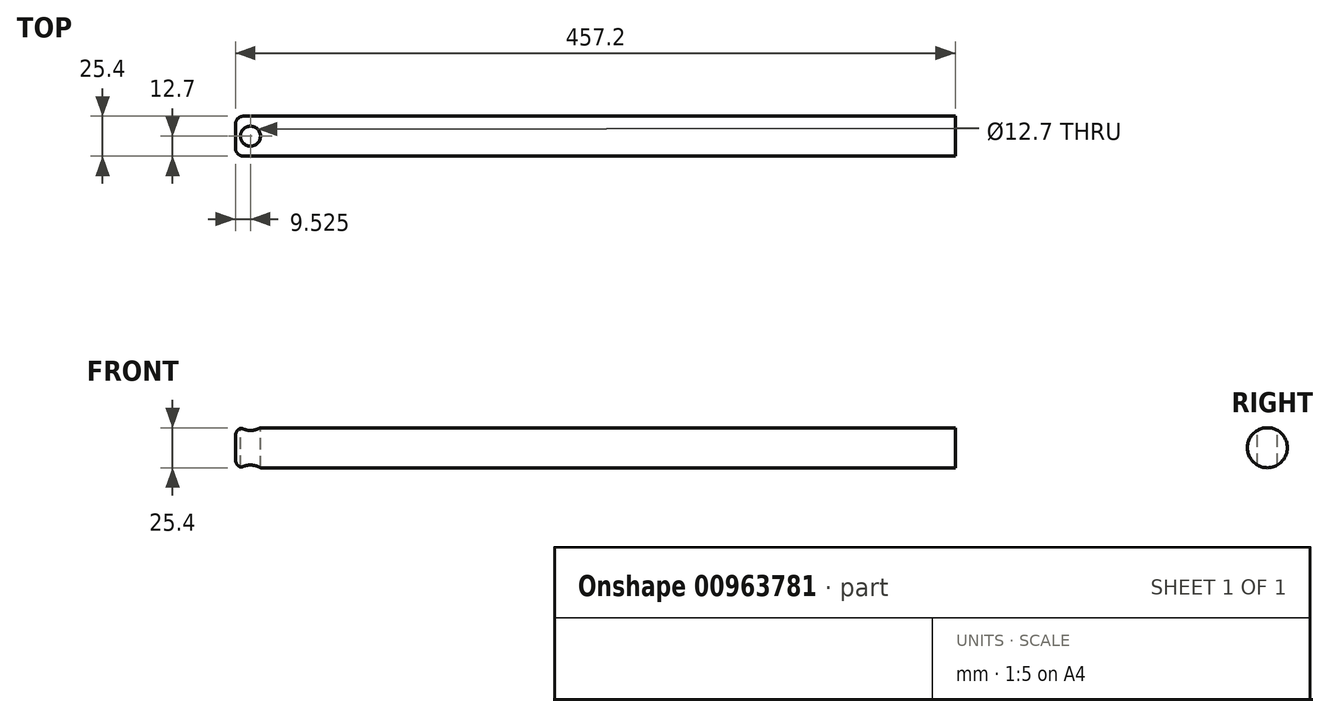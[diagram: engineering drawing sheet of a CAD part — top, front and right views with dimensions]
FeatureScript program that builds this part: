
annotation { "Feature Type Name" : "Feature", "Feature Type Description" : "" }
export const myFeature = defineFeature(function(context is Context, id is Id, definition is map)
    precondition{}
    {
        {
            var Q0;
            Q0=qCreatedBy(makeId("Right.planeOp"),FACE);
            var sketch = newSketch(context, id + "F0", { "sketchPlane" : qUnion([Q0])});
            skCircle(sketch, "E0", {"center": v(0, 0) * mm, "radius": 12.7 * mm});
            skSolve(sketch);
        }
        {
            var Q0;
            Q0 = qSketchRegion(id + "F0", true);
            extrude(context, id + "F1", {"entities" : qUnion([Q0]), "depth" : 457.2 * mm, "offsetDistance" : 25.4 * mm});
        }
        {
            var Q0;
            Q0=qCreatedBy(makeId("Top.planeOp"),FACE);
            var sketch = newSketch(context, id + "F2", { "sketchPlane" : qUnion([Q0])});
            skCircle(sketch, "E1", {"center": v(9.53, 0) * mm, "radius": 6.35 * mm});
            skSolve(sketch);
        }
        {
            var Q0;
            Q0 = qSketchRegion(id + "F2", true);
            extrude(context, id + "F3", {"entities" : qUnion([Q0]), "operationType" : NewBodyOperationType.REMOVE, "endBound" : BoundingType.SYMMETRIC, "oppositeDirection" : true, "depth" : 25.4 * mm, "offsetDistance" : 25.4 * mm});
        }
        {
            var Q0;
            Q0=makeQuery(id+"F1.opExtrude","CAP_EDGE",EDGE,{"disambiguationData":[OSD([sQuery(id+"F0.wireOp",EDGE,"E0")])],"isStart":true});
            fillet(context, id + "F4", {"entities" : qUnion([Q0]), "radius" : 5.08 * mm, "tangentPropagation" : true, "allowEdgeOverflow" : false});
        }
    });
